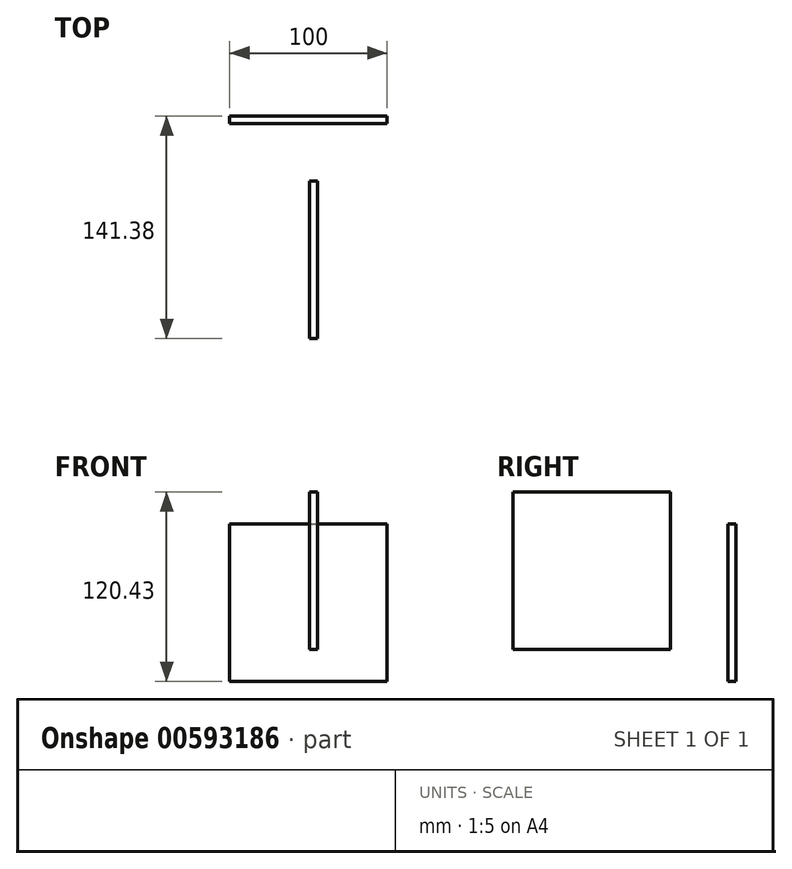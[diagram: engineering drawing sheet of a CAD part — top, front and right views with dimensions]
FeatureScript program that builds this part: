
annotation { "Feature Type Name" : "Feature", "Feature Type Description" : "" }
export const myFeature = defineFeature(function(context is Context, id is Id, definition is map)
    precondition{}
    {
        {
            var Q0;
            Q0=qCreatedBy(makeId("Front.planeOp"),FACE);
            var sketch = newSketch(context, id + "F0", { "sketchPlane" : qUnion([Q0])});
            skLineSegment(sketch, "E0.bottom", {"start": v(-50.83, 49.76) * mm, "end": v(49.17, 49.76) * mm});
            skLineSegment(sketch, "E0.top", {"start": v(-50.83, -50.24) * mm, "end": v(49.17, -50.24) * mm});
            skLineSegment(sketch, "E0.left", {"start": v(-50.83, 49.76) * mm, "end": v(-50.83, -50.24) * mm});
            skLineSegment(sketch, "E0.right", {"start": v(49.17, 49.76) * mm, "end": v(49.17, -50.24) * mm});
            skSolve(sketch);
        }
        {
            var Q0;
            Q0=qCreatedBy(makeId("Right.planeOp"),FACE);
            var sketch = newSketch(context, id + "F1", { "sketchPlane" : qUnion([Q0])});
            skLineSegment(sketch, "E1.bottom", {"start": v(-141.38, 70.19) * mm, "end": v(-41.38, 70.19) * mm});
            skLineSegment(sketch, "E1.top", {"start": v(-141.38, -29.81) * mm, "end": v(-41.38, -29.81) * mm});
            skLineSegment(sketch, "E1.left", {"start": v(-141.38, 70.19) * mm, "end": v(-141.38, -29.81) * mm});
            skLineSegment(sketch, "E1.right", {"start": v(-41.38, 70.19) * mm, "end": v(-41.38, -29.81) * mm});
            skSolve(sketch);
        }
        {
            var Q0;
            Q0 = qSketchRegion(id + "F0", true);
            extrude(context, id + "F2", {"entities" : qUnion([Q0]), "depth" : 5 * mm, "offsetDistance" : 25 * mm});
        }
        {
            var Q0;
            Q0 = qSketchRegion(id + "F1", true);
            extrude(context, id + "F3", {"entities" : qUnion([Q0]), "depth" : 5 * mm, "offsetDistance" : 25 * mm});
        }
    });
